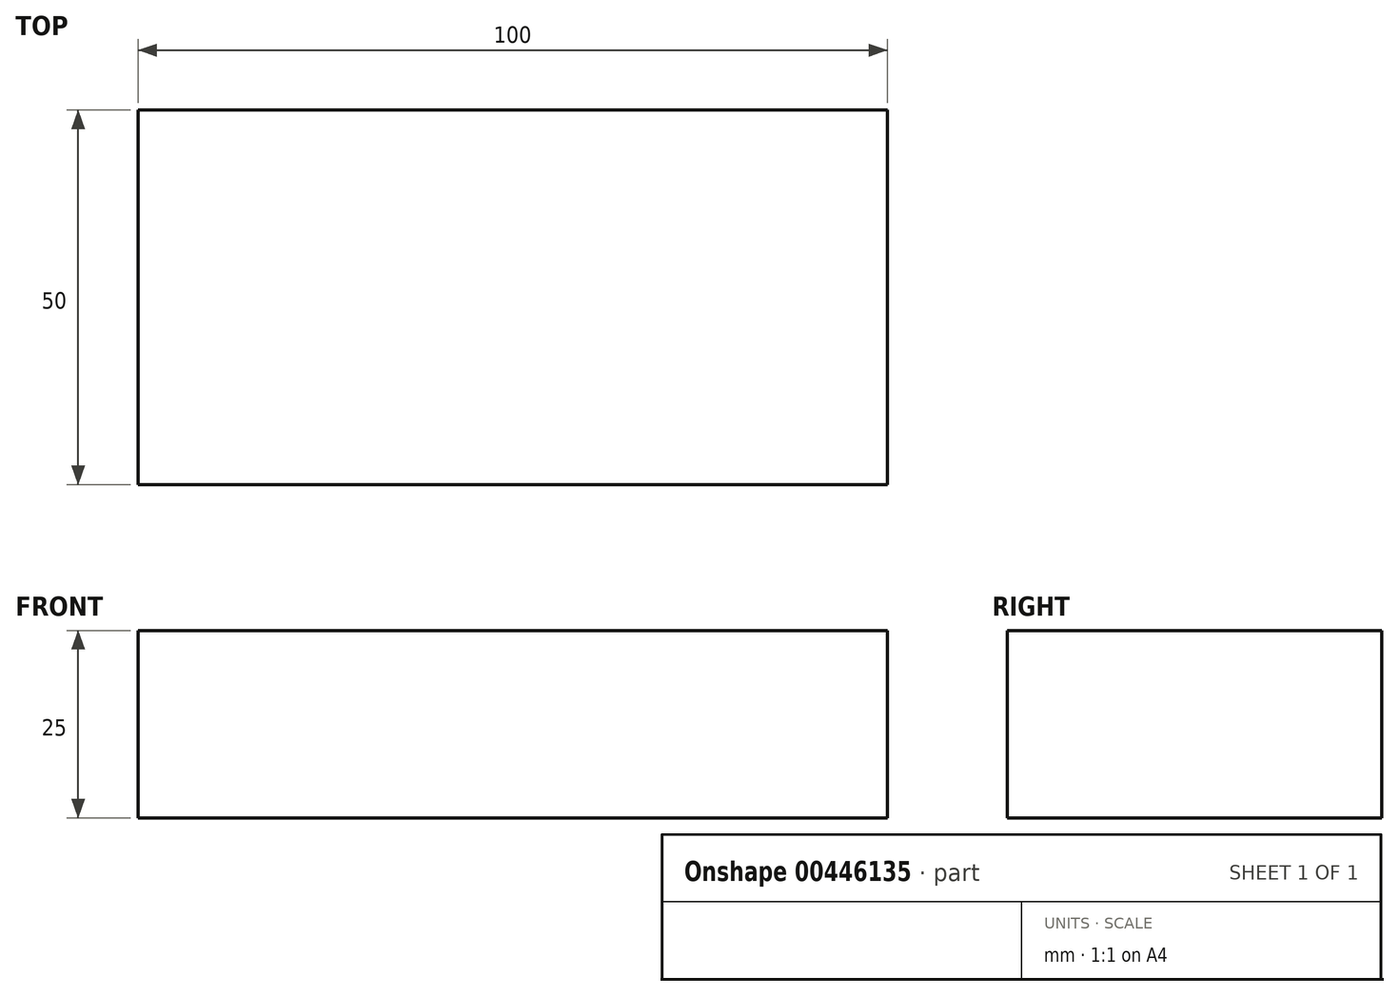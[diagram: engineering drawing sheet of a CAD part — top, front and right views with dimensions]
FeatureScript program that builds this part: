
annotation { "Feature Type Name" : "Feature", "Feature Type Description" : "" }
export const myFeature = defineFeature(function(context is Context, id is Id, definition is map)
    precondition{}
    {
        {
            var Q0;
            Q0=qCreatedBy(makeId("Top.planeOp"),FACE);
            var sketch = newSketch(context, id + "F0", { "sketchPlane" : qUnion([Q0])});
            skLineSegment(sketch, "E0.bottom", {"start": v(-50, 25) * mm, "end": v(50, 25) * mm});
            skLineSegment(sketch, "E0.top", {"start": v(-50, -25) * mm, "end": v(50, -25) * mm});
            skLineSegment(sketch, "E0.left", {"start": v(-50, 25) * mm, "end": v(-50, -25) * mm});
            skLineSegment(sketch, "E0.right", {"start": v(50, 25) * mm, "end": v(50, -25) * mm});
            skSolve(sketch);
        }
        {
            var Q0;
            Q0=makeQuery(id+"F0.imprint","IMPRINT",FACE,{"disambiguationData":[TD([[makeQuery(id+"F0.imprint","IMPRINT",EDGE,{"derivedFrom":sQuery(id+"F0.wireOp",EDGE,"E0.bottom")}),-1.0]])]});
            extrude(context, id + "F1", {"entities" : qUnion([Q0]), "depth" : 25 * mm});
        }
    });
